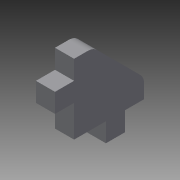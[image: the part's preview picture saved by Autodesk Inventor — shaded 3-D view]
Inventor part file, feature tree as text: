
AUTODESK INVENTOR PART (.ipt)
format: ipt  version: 2013 SP1 (Build 170176100, 176)  size: 88,064 bytes
history: native  units: mm
features: extrude x1, sketch x1
ambient origin geometry x8: Origin, YZ Plane, XZ Plane, XY Plane, X Axis, Y Axis, Z Axis, Center Point
bodies: Solid1 (feature_tree)
feature tree (2):
  extrude  "Extrusion1"  Depth=3.0mm
  sketch  "Sketch1"  dims[d0=5.0mm d1=3.0mm d2=3.0mm d3=5.0mm d4=3.0mm d5=3.0mm d6=3.0mm d7=3.0mm d8=3.0mm d9=3.0mm d10=3.0mm d11=3.0mm d12=3.0mm d13=0.0mm d14=2.0mm]
